# Revit family: cbc4e2c1-9cd4-4468-acf4-dc7168def20e
name_source: partatom
category: Generic Models
revit_build: Autodesk Revit Architecture 2012 (Build: 20110916_2132(x64)
units: mm (PartAtom-declared; Revit-internal decimal feet)

## types (3) — shared parameters
Assembly Code = E1090900
Capacity = 1000 lbs per rung
Default Elevation = 4' - 0"
Description = UPNOVR U-201 Roof Access Vertical Aluminum Ladder
Frame Material = Metal - UPNOVR - 6061-T6 Aluminum
Green Building-LEED = http://www.arcat.com
Keynote = 05510
Manufacturer = UPNOVR, Inc.
Manufacturer Website = http://www.aclindustries.com
Model = U-201
Product Data = http://www.arcat.com
Revision = R1_04-2013
Sales Information = http://www.aclindustries.com
Send Message = http://www.arcat.com
Standards Conformance = OSHA and ANSI A14.3
URL = http://www.aclindustries.com
zero-valued in all types: Expected Lifespan (Years), Maintenance Schedule (Months), Warranty Duration (Years)

## per-type parameters (varying)
| type | Unit Width |
| 24"" Wide | 2' - 0" |
| 18"" Wide Gooseneck | 1' - 6" |
| 18"" Wide | 1' - 6" |

## geometry (parser evidence)
native form markers: Blend x2, Sweep x5
no freeform markers — native parametric forms only
